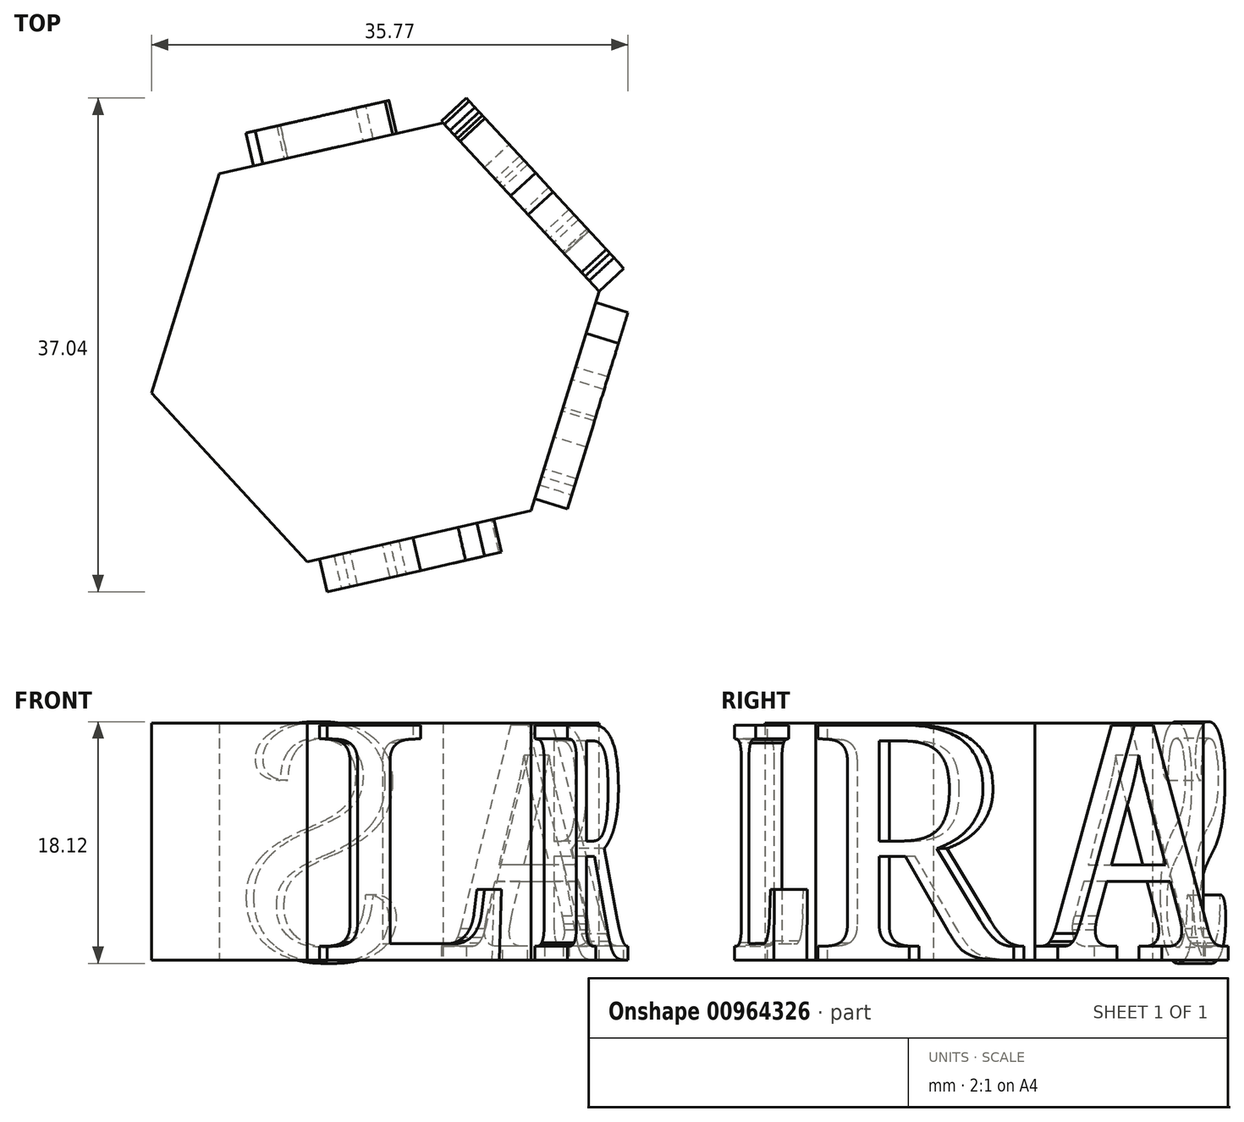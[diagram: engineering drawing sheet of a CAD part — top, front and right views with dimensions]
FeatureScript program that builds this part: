
annotation { "Feature Type Name" : "Feature", "Feature Type Description" : "" }
export const myFeature = defineFeature(function(context is Context, id is Id, definition is map)
    precondition{}
    {
        {
            var Q0;
            Q0=qCreatedBy(makeId("Top.planeOp"),FACE);
            var sketch = newSketch(context, id + "F0", { "sketchPlane" : qUnion([Q0])});
            skCircle(sketch, "E0.cCircle", {"center": v(0, 0) * mm, "radius": 14.92 * mm, "construction": true});
            skLineSegment(sketch, "E0.0", {"start": v(11.7, -12.64) * mm, "end": v(-5.1, -16.46) * mm});
            skLineSegment(sketch, "E0.1", {"start": v(-5.1, -16.46) * mm, "end": v(-16.8, -3.82) * mm});
            skLineSegment(sketch, "E0.2", {"start": v(-16.8, -3.82) * mm, "end": v(-11.7, 12.64) * mm});
            skLineSegment(sketch, "E0.3", {"start": v(-11.7, 12.64) * mm, "end": v(5.1, 16.46) * mm});
            skLineSegment(sketch, "E0.4", {"start": v(5.1, 16.46) * mm, "end": v(16.8, 3.82) * mm});
            skLineSegment(sketch, "E0.5", {"start": v(16.8, 3.82) * mm, "end": v(11.7, -12.64) * mm});
            skPoint(sketch, "E0.0.midPoint", {"position": v(3.3, -14.55) * mm});
            skSolve(sketch);
        }
        {
            var Q0;
            Q0=makeQuery(id+"F0.imprint","IMPRINT",FACE,{"disambiguationData":[TD([[makeQuery(id+"F0.imprint","IMPRINT",EDGE,{"derivedFrom":sQuery(id+"F0.wireOp",EDGE,"E0.0")}),-1.0]])]});
            extrude(context, id + "F1", {"entities" : qUnion([Q0]), "depth" : 17.78 * mm, "offsetDistance" : 25.4 * mm});
        }
        {
            var Q0;
            Q0=makeQuery(id+"F1.opExtrude","SWEPT_FACE",FACE,{"disambiguationData":[OSD([sQuery(id+"F0.wireOp",EDGE,"E0.0")])]});
            var sketch = newSketch(context, id + "F2", { "sketchPlane" : qUnion([Q0])});
            skText(sketch, "E1", { "text": "L", "fontName": "NotoSerif-Regular.ttf"});
            const initialGuessF2  = {"E1": [-0.00861, 0, 1, 0, 0.01778]};
            skSetInitialGuess(sketch, initialGuessF2);
            skSolve(sketch);
        }
        {
            var Q0;
            Q0 = qSketchRegion(id + "F2", true);
            extrude(context, id + "F3", {"entities" : qUnion([Q0]), "operationType" : NewBodyOperationType.ADD, "depth" : 2.54 * mm, "offsetDistance" : 25.4 * mm});
        }
        {
            var Q0;
            Q0=makeQuery(id+"F1.opExtrude","SWEPT_FACE",FACE,{"disambiguationData":[OSD([sQuery(id+"F0.wireOp",EDGE,"E0.5")])]});
            var sketch = newSketch(context, id + "F4", { "sketchPlane" : qUnion([Q0])});
            skText(sketch, "E2", { "text": "R", "fontName": "NotoSerif-Regular.ttf"});
            const initialGuessF4  = {"E2": [-0.00861, 0, 1, 0, 0.01778]};
            skSetInitialGuess(sketch, initialGuessF4);
            skSolve(sketch);
        }
        {
            var Q0;
            Q0 = qSketchRegion(id + "F4", true);
            extrude(context, id + "F5", {"entities" : qUnion([Q0]), "operationType" : NewBodyOperationType.ADD, "depth" : 2.54 * mm, "offsetDistance" : 25.4 * mm});
        }
        {
            var Q0;
            Q0=qCreatedBy(makeId("Front.planeOp"),FACE);
            var sketch = newSketch(context, id + "F6", { "sketchPlane" : qUnion([Q0])});
            skText(sketch, "E3", { "text": "A", "fontName": "NotoSerif-Regular.ttf"});
            const initialGuessF6  = {"E3": [-0.00567, 0, 1, 0, 0.01776]};
            skSetInitialGuess(sketch, initialGuessF6);
            skSolve(sketch);
        }
        {
            var Q0;
            Q0 = qSketchRegion(id + "F6", true);
            extrude(context, id + "F7", {"entities" : qUnion([Q0]), "operationType" : NewBodyOperationType.ADD, "depth" : 2.54 * mm, "offsetDistance" : 25.4 * mm});
        }
        {
            var Q0;
            Q0=makeQuery(id+"F1.opExtrude","SWEPT_FACE",FACE,{"disambiguationData":[OSD([sQuery(id+"F0.wireOp",EDGE,"E0.4")])]});
            var sketch = newSketch(context, id + "F8", { "sketchPlane" : qUnion([Q0])});
            skText(sketch, "E4", { "text": "A", "fontName": "NotoSerif-Regular.ttf"});
            const initialGuessF8  = {"E4": [-0.00861, 0, 1, 0, 0.01778]};
            skSetInitialGuess(sketch, initialGuessF8);
            skSolve(sketch);
        }
        {
            var Q0;
            Q0 = qSketchRegion(id + "F8", true);
            extrude(context, id + "F9", {"entities" : qUnion([Q0]), "operationType" : NewBodyOperationType.ADD, "depth" : 2.54 * mm, "offsetDistance" : 25.4 * mm});
        }
        {
            var Q0;
            Q0=makeQuery(id+"F1.opExtrude","SWEPT_FACE",FACE,{"disambiguationData":[OSD([sQuery(id+"F0.wireOp",EDGE,"E0.3")])]});
            var sketch = newSketch(context, id + "F10", { "sketchPlane" : qUnion([Q0])});
            skText(sketch, "E5", { "text": "S", "fontName": "NotoSerif-Regular.ttf"});
            const initialGuessF10  = {"E5": [-0.0062, 0, 1, 0, 0.01778]};
            skSetInitialGuess(sketch, initialGuessF10);
            skSolve(sketch);
        }
        {
            var Q0;
            Q0 = qSketchRegion(id + "F10", true);
            extrude(context, id + "F11", {"entities" : qUnion([Q0]), "operationType" : NewBodyOperationType.ADD, "depth" : 2.54 * mm, "offsetDistance" : 25.4 * mm});
        }
    });
